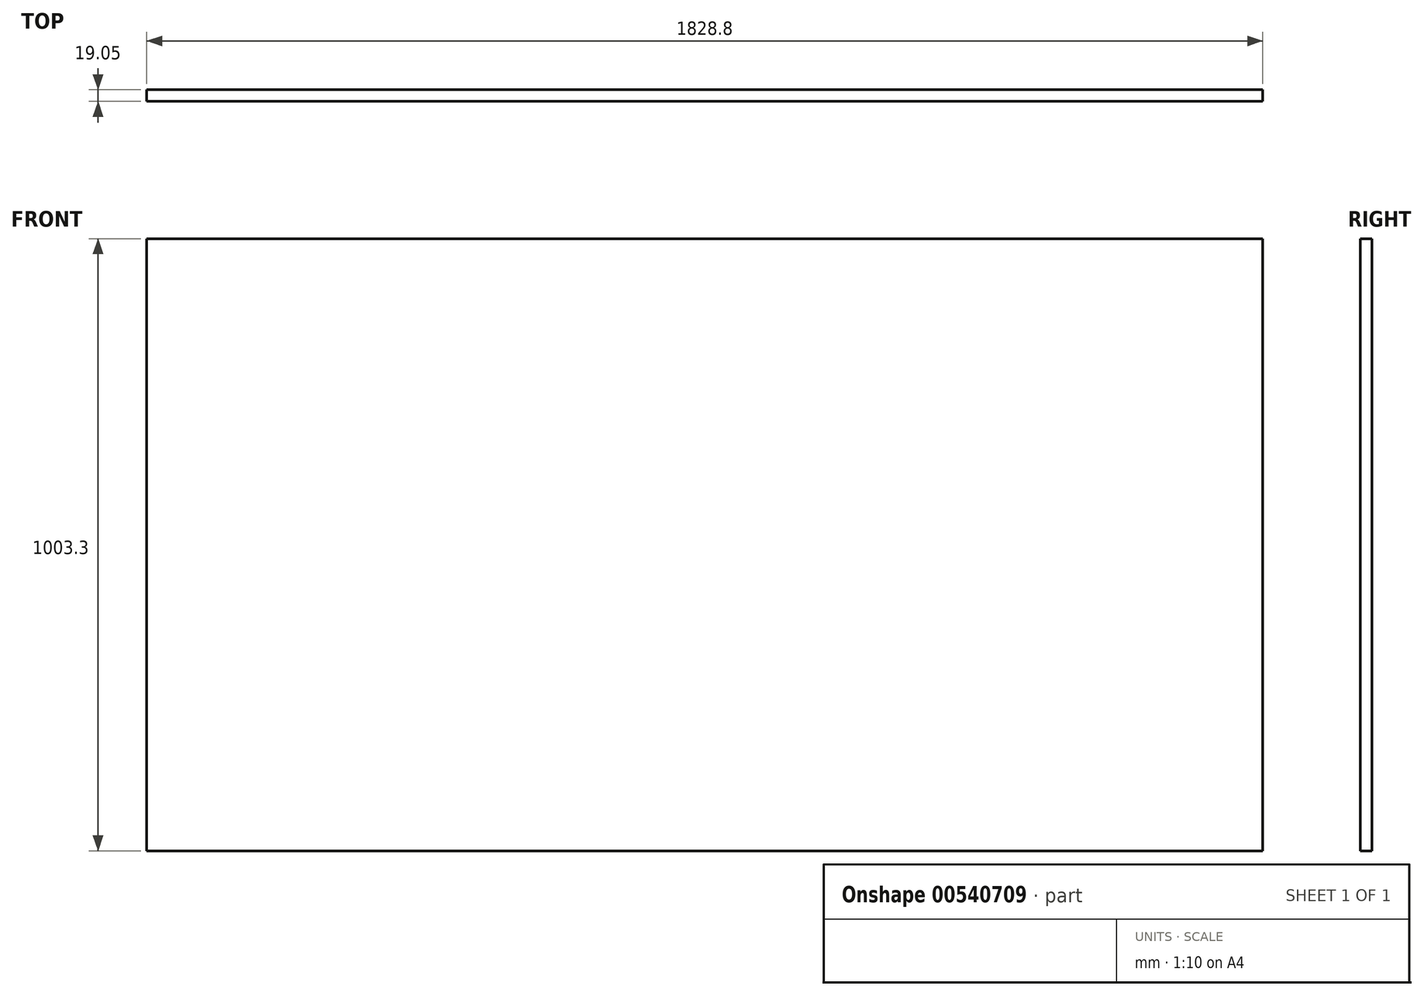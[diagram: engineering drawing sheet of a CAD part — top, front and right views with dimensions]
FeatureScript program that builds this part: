
annotation { "Feature Type Name" : "Feature", "Feature Type Description" : "" }
export const myFeature = defineFeature(function(context is Context, id is Id, definition is map)
    precondition{}
    {
        {
            var Q0;
            Q0=qCreatedBy(makeId("Front.planeOp"),FACE);
            var sketch = newSketch(context, id + "F0", { "sketchPlane" : qUnion([Q0])});
            skLineSegment(sketch, "E0.bottom", {"start": v(914.4, 501.65) * mm, "end": v(-914.4, 501.65) * mm});
            skLineSegment(sketch, "E0.top", {"start": v(914.4, -501.65) * mm, "end": v(-914.4, -501.65) * mm});
            skLineSegment(sketch, "E0.left", {"start": v(914.4, 501.65) * mm, "end": v(914.4, -501.65) * mm});
            skLineSegment(sketch, "E0.right", {"start": v(-914.4, 501.65) * mm, "end": v(-914.4, -501.65) * mm});
            skPoint(sketch, "E0.middle", {"position": v(0, 0) * mm});
            skSolve(sketch);
        }
        {
            var Q0;
            Q0=makeQuery(id+"F0.imprint","IMPRINT",FACE,{"disambiguationData":[TD([[makeQuery(id+"F0.imprint","IMPRINT",EDGE,{"derivedFrom":sQuery(id+"F0.wireOp",EDGE,"E0.bottom")}),1.0]])]});
            extrude(context, id + "F1", {"entities" : qUnion([Q0]), "depth" : 19.05 * mm, "offsetDistance" : 25.4 * mm});
        }
    });
